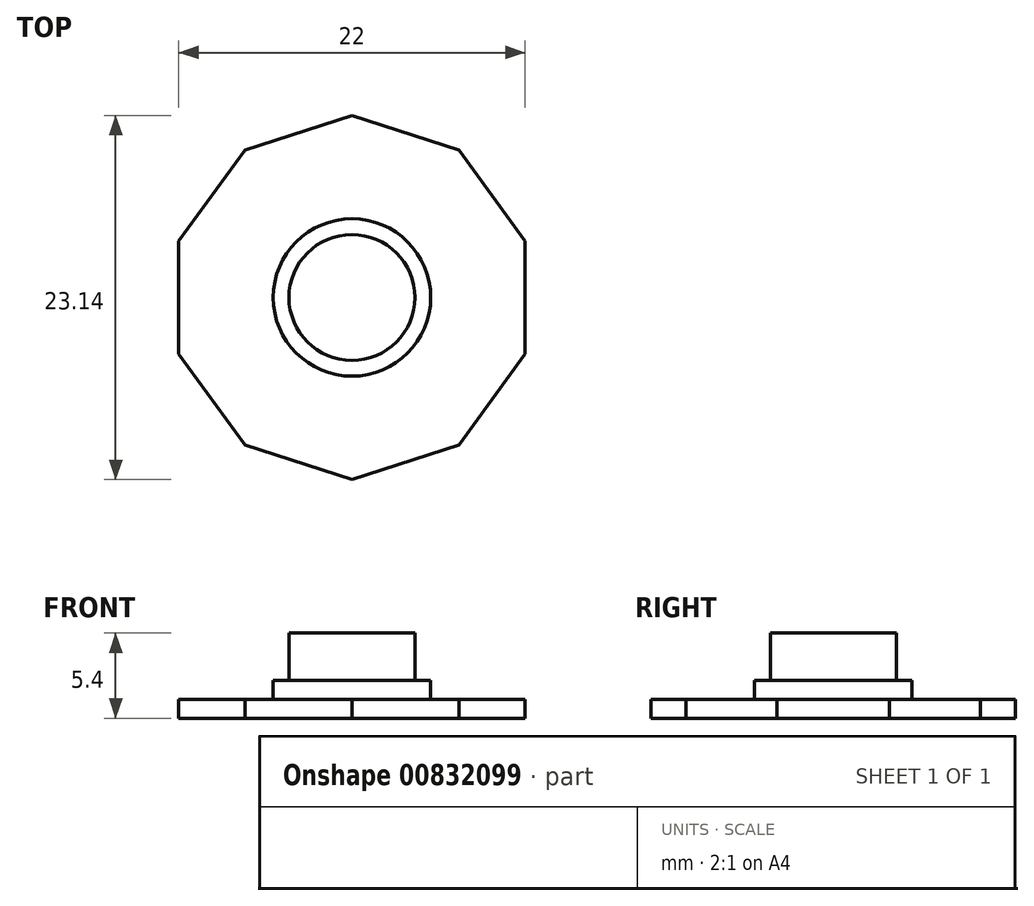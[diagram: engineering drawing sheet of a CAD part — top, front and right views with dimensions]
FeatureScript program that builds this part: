
annotation { "Feature Type Name" : "Feature", "Feature Type Description" : "" }
export const myFeature = defineFeature(function(context is Context, id is Id, definition is map)
    precondition{}
    {
        {
            var Q0;
            Q0=qCreatedBy(makeId("Top.planeOp"),FACE);
            var sketch = newSketch(context, id + "F0", { "sketchPlane" : qUnion([Q0])});
            skCircle(sketch, "E0.cCircle", {"center": v(0, 0) * mm, "radius": 11 * mm, "construction": true});
            skLineSegment(sketch, "E0.0", {"start": v(-11, -3.57) * mm, "end": v(-11, 3.57) * mm});
            skLineSegment(sketch, "E0.1", {"start": v(-11, 3.57) * mm, "end": v(-6.8, 9.36) * mm});
            skLineSegment(sketch, "E0.2", {"start": v(-6.8, 9.36) * mm, "end": v(0, 11.57) * mm});
            skLineSegment(sketch, "E0.3", {"start": v(0, 11.57) * mm, "end": v(6.8, 9.36) * mm});
            skLineSegment(sketch, "E0.4", {"start": v(6.8, 9.36) * mm, "end": v(11, 3.57) * mm});
            skLineSegment(sketch, "E0.5", {"start": v(11, 3.57) * mm, "end": v(11, -3.57) * mm});
            skLineSegment(sketch, "E0.6", {"start": v(11, -3.57) * mm, "end": v(6.8, -9.36) * mm});
            skLineSegment(sketch, "E0.7", {"start": v(6.8, -9.36) * mm, "end": v(0, -11.57) * mm});
            skLineSegment(sketch, "E0.8", {"start": v(0, -11.57) * mm, "end": v(-6.8, -9.36) * mm});
            skLineSegment(sketch, "E0.9", {"start": v(-6.8, -9.36) * mm, "end": v(-11, -3.57) * mm});
            skPoint(sketch, "E0.0.midPoint", {"position": v(-11, 0) * mm});
            skSolve(sketch);
        }
        {
            var Q0;
            Q0=makeQuery(id+"F0.imprint","IMPRINT",FACE,{"disambiguationData":[TD([[makeQuery(id+"F0.imprint","IMPRINT",EDGE,{"derivedFrom":sQuery(id+"F0.wireOp",EDGE,"E0.0")}),-1.0]])]});
            extrude(context, id + "F1", {"entities" : qUnion([Q0]), "depth" : 1.2 * mm, "offsetDistance" : 25.4 * mm});
        }
        {
            var Q0;
            Q0=makeQuery(id+"F1.opExtrude","CAP_FACE",FACE,{"disambiguationData":[OSD([sQuery(id+"F0.wireOp",EDGE,"E0.0"),sQuery(id+"F0.wireOp",EDGE,"E0.1"),sQuery(id+"F0.wireOp",EDGE,"E0.2"),sQuery(id+"F0.wireOp",EDGE,"E0.3"),sQuery(id+"F0.wireOp",EDGE,"E0.4"),sQuery(id+"F0.wireOp",EDGE,"E0.5"),sQuery(id+"F0.wireOp",EDGE,"E0.6"),sQuery(id+"F0.wireOp",EDGE,"E0.7"),sQuery(id+"F0.wireOp",EDGE,"E0.8"),sQuery(id+"F0.wireOp",EDGE,"E0.9")])],"isStart":false});
            var sketch = newSketch(context, id + "F2", { "sketchPlane" : qUnion([Q0])});
            skCircle(sketch, "E1", {"center": v(0, 0) * mm, "radius": 5 * mm});
            skSolve(sketch);
        }
        {
            var Q0;
            Q0=makeQuery(id+"F2.imprint","IMPRINT",FACE,{"disambiguationData":[TD([[makeQuery(id+"F2.imprint","IMPRINT",EDGE,{"derivedFrom":sQuery(id+"F2.wireOp",EDGE,"E1")}),1.0]])]});
            extrude(context, id + "F3", {"entities" : qUnion([Q0]), "operationType" : NewBodyOperationType.ADD, "depth" : 1.2 * mm, "offsetDistance" : 25 * mm});
        }
        {
            var Q0;
            Q0=makeQuery(id+"F3.opExtrude","CAP_FACE",FACE,{"disambiguationData":[OSD([sQuery(id+"F2.wireOp",EDGE,"E1")])],"isStart":false});
            var sketch = newSketch(context, id + "F4", { "sketchPlane" : qUnion([Q0])});
            skCircle(sketch, "E2", {"center": v(0, 0) * mm, "radius": 4 * mm});
            skSolve(sketch);
        }
        {
            var Q0;
            Q0=makeQuery(id+"F4.imprint","IMPRINT",FACE,{"disambiguationData":[TD([[makeQuery(id+"F4.imprint","IMPRINT",EDGE,{"derivedFrom":sQuery(id+"F4.wireOp",EDGE,"E2")}),1.0]])]});
            extrude(context, id + "F5", {"entities" : qUnion([Q0]), "operationType" : NewBodyOperationType.ADD, "depth" : 3 * mm, "offsetDistance" : 25 * mm});
        }
    });
